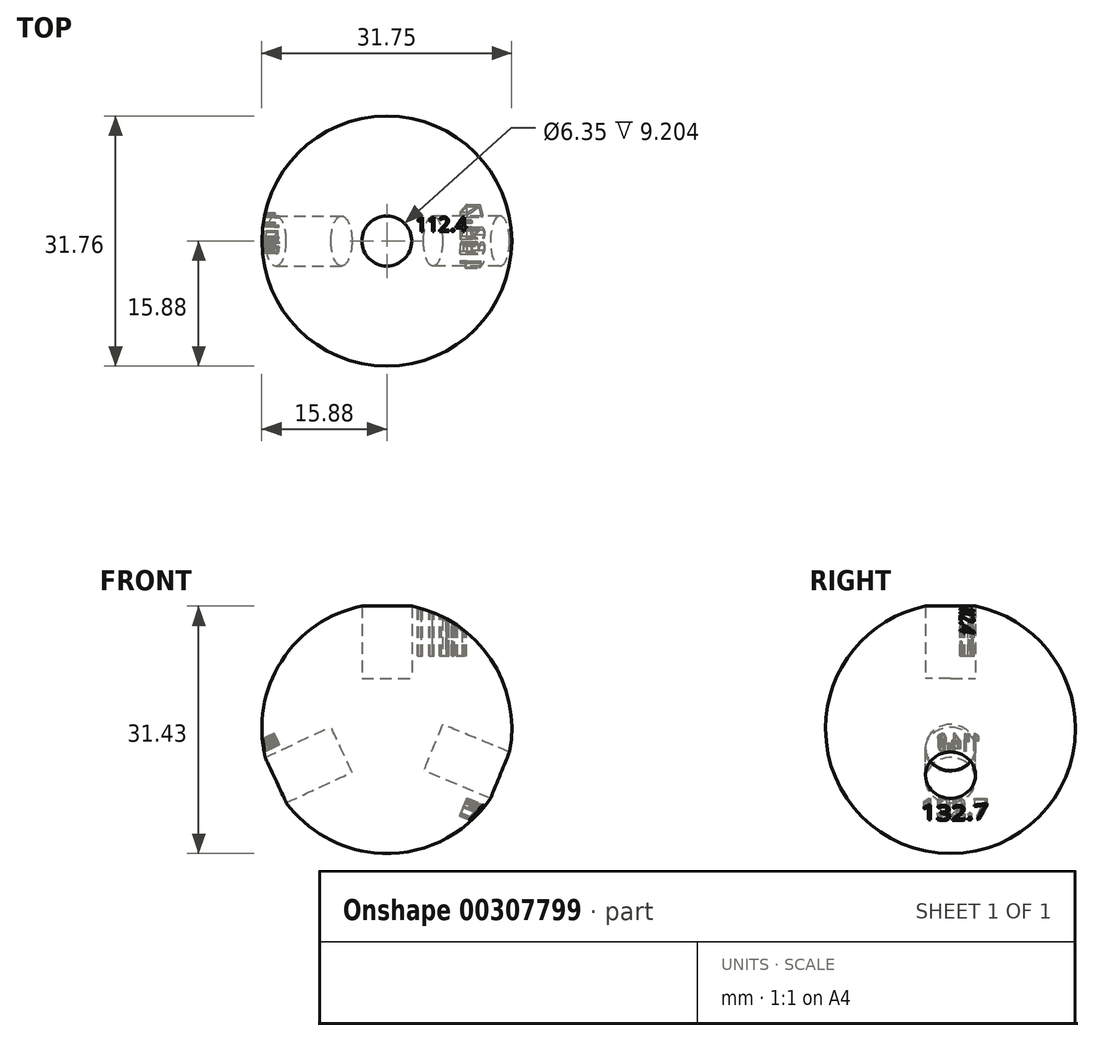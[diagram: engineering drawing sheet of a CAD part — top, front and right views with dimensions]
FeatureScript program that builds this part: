
annotation { "Feature Type Name" : "Feature", "Feature Type Description" : "" }
export const myFeature = defineFeature(function(context is Context, id is Id, definition is map)
    precondition{}
    {
        {
            var Q0;
            Q0=qCreatedBy(makeId("Top.planeOp"),FACE);
            var sketch = newSketch(context, id + "F0", { "sketchPlane" : qUnion([Q0])});
            skLineSegment(sketch, "E0", {"start": v(0, 0) * mm, "end": v(0, 66.55) * mm, "construction": true});
            skLineSegment(sketch, "E1", {"start": v(0, 0) * mm, "end": v(-79.64, 0) * mm, "construction": true});
            skSolve(sketch);
        }
        {
            var Q0;
            Q0=qCreatedBy(makeId("Top.planeOp"),FACE);
            var sketch = newSketch(context, id + "F1", { "sketchPlane" : qUnion([Q0])});
            skArc(sketch, "E2", {"start": v(0, 15.88) * mm, "mid": v(-15.88, 0) * mm, "end": v(0, -15.88) * mm});
            skLineSegment(sketch, "E3", {"start": v(0, 15.88) * mm, "end": v(0, -15.88) * mm});
            skSolve(sketch);
        }
        {
            var Q0;
            Q0=makeQuery(id+"F1.imprint","IMPRINT",FACE,{"disambiguationData":[TD([[makeQuery(id+"F1.imprint","IMPRINT",EDGE,{"derivedFrom":sQuery(id+"F1.wireOp",EDGE,"E2")}),1.0]])]});
            var Q1;
            Q1=sQuery(id+"F1.wireOp",EDGE,"E3");
            revolve(context, id + "F2", {"entities" : qUnion([Q0]), "axis" : qUnion([Q1]), "revolveType" : RevolveType.FULL});
        }
        {
            var Q0;
            Q0=qCreatedBy(makeId("Top.planeOp"),FACE);
            cPlane(context, id + "F3", {"entities" : qUnion([Q0]), "cplaneType" : CPlaneType.OFFSET, "offset" : 6.35 * mm, "width" : 152.4 * mm, "height" : 152.4 * mm});
        }
        {
            var Q0;
            Q0=qCreatedBy(id+"F3.planeOp",FACE);
            var sketch = newSketch(context, id + "F4", { "sketchPlane" : qUnion([Q0])});
            skCircle(sketch, "E4", {"center": v(0, 0) * mm, "radius": 3.18 * mm});
            skSolve(sketch);
        }
        {
            var Q0;
            Q0 = qSketchRegion(id + "F4", true);
            extrude(context, id + "F5", {"entities" : qUnion([Q0]), "depth" : 25.4 * mm});
        }
        {
            var Q0;
            Q0=makeQuery(id+"F5.opExtrude","CAP_FACE",FACE,{"disambiguationData":[OSD([sQuery(id+"F4.wireOp",EDGE,"E4")])],"isStart":false});
            cPlane(context, id + "F6", {"entities" : qUnion([Q0]), "cplaneType" : CPlaneType.OFFSET, "offset" : 14.66 * mm, "oppositeDirection" : true, "width" : 152.4 * mm, "height" : 152.4 * mm});
        }
        {
            var Q0;
            Q0=qCreatedBy(id+"F6.planeOp",FACE);
            var sketch = newSketch(context, id + "F7", { "sketchPlane" : qUnion([Q0])});
            skText(sketch, "E5", { "text": "112.4", "fontName": "OpenSans-Regular.ttf"});
            const initialGuessF7  = {"E5": [0.00368, 0.00122, 1, 0, 0.00183]};
            skSetInitialGuess(sketch, initialGuessF7);
            skSolve(sketch);
        }
        {
            var Q0;
            Q0 = qSketchRegion(id + "F7", true);
            extrude(context, id + "F8", {"entities" : qUnion([Q0]), "operationType" : NewBodyOperationType.REMOVE, "oppositeDirection" : true, "depth" : 7.9 * mm});
        }
        {
            var Q0;
            Q0=makeQuery(id+"F5.opExtrude","SWEPT_BODY",BODY,{"disambiguationData":[OSD([sQuery(id+"F4.wireOp",EDGE,"E4")])]});
            var Q1;
            Q1=sQuery(id+"F0.wireOp",EDGE,"E0");
            var Q2;
            Q2=sQuery(id+"F0.wireOp",EDGE,"E0");
            transform(context, id + "F9", {"entities" : qUnion([Q0]), "transformType" : TransformType.ROTATION, "transformAxis" : qUnion([Q2]), "angle" : 112.4 * degree, "makeCopy" : true});
        }
        {
            var Q0;
            Q0=makeQuery(id+"F9.opPattern","COPY",BODY,{"derivedFrom":makeQuery(id+"F5.opExtrude","SWEPT_BODY",BODY,{"disambiguationData":[OSD([sQuery(id+"F4.wireOp",EDGE,"E4")])]}),"instanceName":"1"});
            var Q1;
            Q1=sQuery(id+"F0.wireOp",EDGE,"E0");
            var Q2;
            Q2=sQuery(id+"F0.wireOp",EDGE,"E0");
            transform(context, id + "F10", {"entities" : qUnion([Q0]), "transformType" : TransformType.ROTATION, "transformAxis" : qUnion([Q2]), "angle" : 132.7 * degree, "makeCopy" : true});
        }
        {
            var Q0;
            Q0=makeQuery(id+"F9.opPattern","COPY",FACE,{"derivedFrom":makeQuery(id+"F5.opExtrude","CAP_FACE",FACE,{"disambiguationData":[OSD([sQuery(id+"F4.wireOp",EDGE,"E4")])],"isStart":false}),"instanceName":"1"});
            cPlane(context, id + "F11", {"entities" : qUnion([Q0]), "cplaneType" : CPlaneType.OFFSET, "offset" : 12.7 * mm, "oppositeDirection" : true, "width" : 152.4 * mm, "height" : 152.4 * mm});
        }
        {
            var Q0;
            Q0=qCreatedBy(id+"F11.planeOp",FACE);
            var sketch = newSketch(context, id + "F12", { "sketchPlane" : qUnion([Q0])});
            skText(sketch, "E6", { "text": "132.7", "fontName": "OpenSans-Regular.ttf"});
            const initialGuessF12  = {"E6": [-0.00373, -0.0067, 1, 0, 0.00241]};
            skSetInitialGuess(sketch, initialGuessF12);
            skSolve(sketch);
        }
        {
            var Q0;
            Q0 = qSketchRegion(id + "F12", true);
            extrude(context, id + "F13", {"entities" : qUnion([Q0]), "operationType" : NewBodyOperationType.REMOVE, "oppositeDirection" : true, "depth" : 6.25 * mm});
        }
        {
            var Q0;
            Q0=makeQuery(id+"F10.opPattern","COPY",FACE,{"derivedFrom":makeQuery(id+"F9.opPattern","COPY",FACE,{"derivedFrom":makeQuery(id+"F5.opExtrude","CAP_FACE",FACE,{"disambiguationData":[OSD([sQuery(id+"F4.wireOp",EDGE,"E4")])],"isStart":false}),"instanceName":"1"}),"instanceName":"1"});
            cPlane(context, id + "F14", {"entities" : qUnion([Q0]), "cplaneType" : CPlaneType.OFFSET, "offset" : 12.7 * mm, "oppositeDirection" : true, "width" : 152.4 * mm, "height" : 152.4 * mm});
        }
        {
            var Q0;
            Q0=qCreatedBy(id+"F14.planeOp",FACE);
            var sketch = newSketch(context, id + "F15", { "sketchPlane" : qUnion([Q0])});
            skText(sketch, "E7", { "text": "114.9", "fontName": "OpenSans-Regular.ttf"});
            const initialGuessF15  = {"E7": [-0.00374, 0.0039, 1, 0, 0.00154]};
            skSetInitialGuess(sketch, initialGuessF15);
            skSolve(sketch);
        }
        {
            var Q0;
            Q0 = qSketchRegion(id + "F15", true);
            extrude(context, id + "F16", {"entities" : qUnion([Q0]), "operationType" : NewBodyOperationType.REMOVE, "oppositeDirection" : true, "depth" : 5.8 * mm});
        }
        {
            var Q0;
            Q0=makeQuery(id+"F5.opExtrude","SWEPT_BODY",BODY,{"disambiguationData":[OSD([sQuery(id+"F4.wireOp",EDGE,"E4")])]});
            var Q1;
            Q1=makeQuery(id+"F10.opPattern","COPY",BODY,{"derivedFrom":makeQuery(id+"F9.opPattern","COPY",BODY,{"derivedFrom":makeQuery(id+"F5.opExtrude","SWEPT_BODY",BODY,{"disambiguationData":[OSD([sQuery(id+"F4.wireOp",EDGE,"E4")])]}),"instanceName":"1"}),"instanceName":"1"});
            var Q2;
            Q2=makeQuery(id+"F9.opPattern","COPY",BODY,{"derivedFrom":makeQuery(id+"F5.opExtrude","SWEPT_BODY",BODY,{"disambiguationData":[OSD([sQuery(id+"F4.wireOp",EDGE,"E4")])]}),"instanceName":"1"});
            var Q3;
            Q3=makeQuery(id+"F2.opRevolve","SWEPT_BODY",BODY,{"disambiguationData":[OSD([sQuery(id+"F1.wireOp",EDGE,"E2"),sQuery(id+"F1.wireOp",EDGE,"E3")])]});
            booleanBodies(context, id + "F17", {"operationType" : BooleanOperationType.SUBTRACTION, "tools" : qUnion([Q0, Q1, Q2]), "targets" : qUnion([Q3])});
        }
    });
